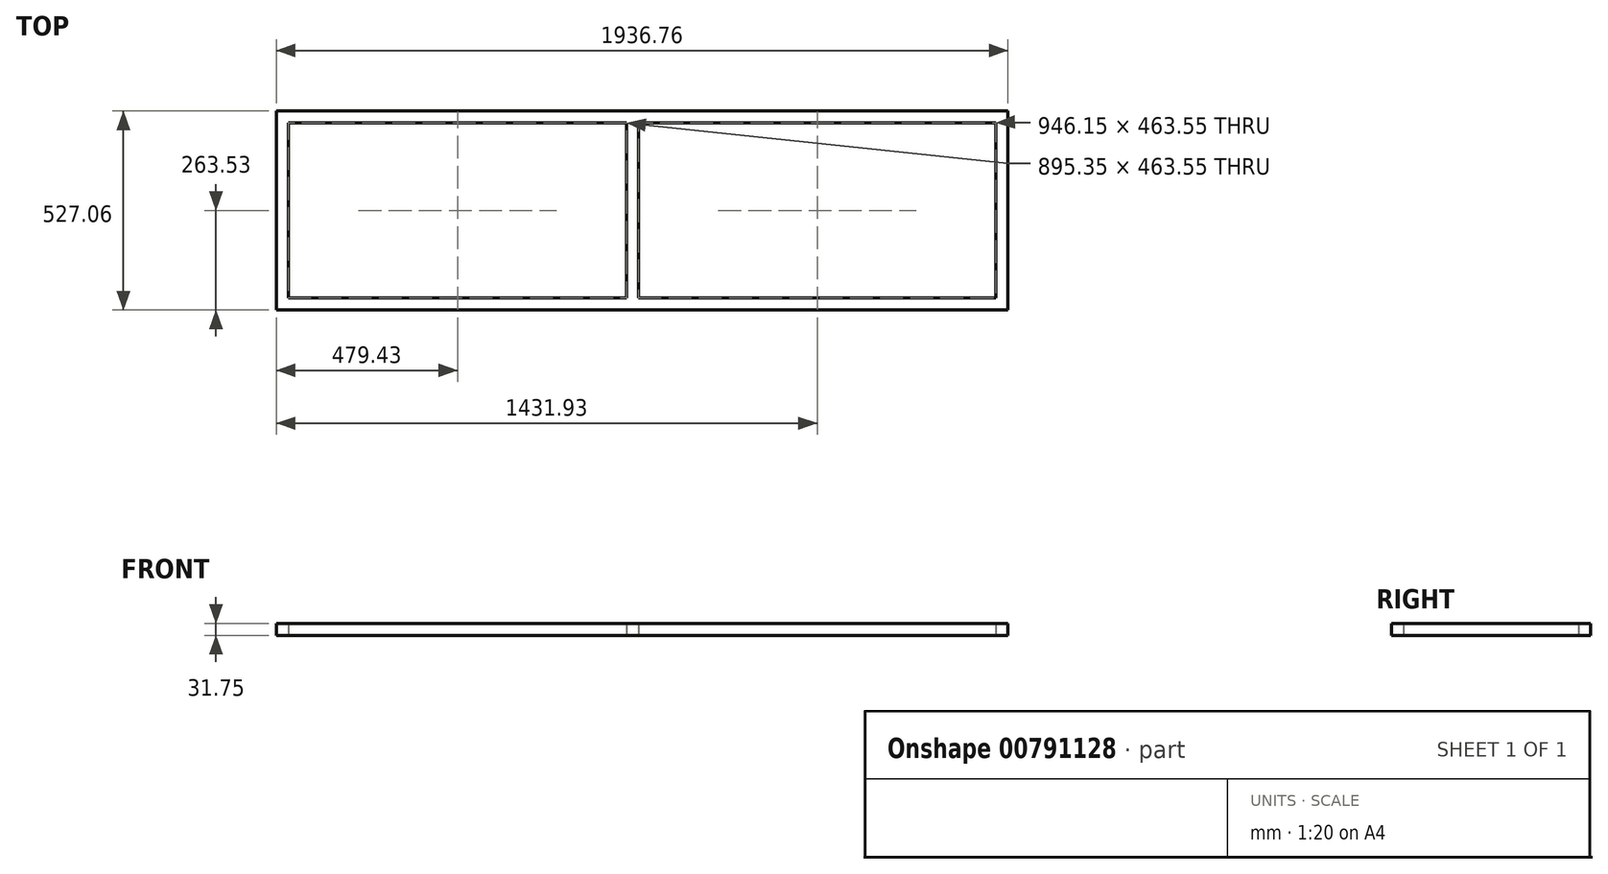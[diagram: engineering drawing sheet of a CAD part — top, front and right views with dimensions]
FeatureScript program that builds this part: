
annotation { "Feature Type Name" : "Feature", "Feature Type Description" : "" }
export const myFeature = defineFeature(function(context is Context, id is Id, definition is map)
    precondition{}
    {
        {
            var Q0;
            Q0=qCreatedBy(makeId("Top.planeOp"),FACE);
            cPlane(context, id + "F0", {"entities" : qUnion([Q0]), "cplaneType" : CPlaneType.OFFSET, "offset" : 254 * mm, "width" : 152.4 * mm, "height" : 152.4 * mm});
        }
        {
            var Q0;
            Q0=qCreatedBy(id+"F0.planeOp",FACE);
            var sketch = newSketch(context, id + "F1", { "sketchPlane" : qUnion([Q0])});
            skLineSegment(sketch, "E0.bottom", {"start": v(447.68, 231.77) * mm, "end": v(-447.68, 231.77) * mm});
            skLineSegment(sketch, "E0.top", {"start": v(447.68, -231.77) * mm, "end": v(-447.68, -231.77) * mm});
            skLineSegment(sketch, "E0.left", {"start": v(447.68, 231.78) * mm, "end": v(447.68, -231.78) * mm});
            skLineSegment(sketch, "E0.right", {"start": v(-447.68, 231.77) * mm, "end": v(-447.68, -231.77) * mm});
            skPoint(sketch, "E0.middle", {"position": v(0, 0) * mm});
            skLineSegment(sketch, "E1.bottom", {"start": v(479.43, 263.53) * mm, "end": v(-479.43, 263.52) * mm});
            skLineSegment(sketch, "E1.top", {"start": v(479.43, -263.52) * mm, "end": v(-479.43, -263.53) * mm});
            skLineSegment(sketch, "E1.right", {"start": v(-479.43, 263.52) * mm, "end": v(-479.43, -263.53) * mm});
            skLineSegment(sketch, "E2.bottom", {"start": v(479.43, -263.52) * mm, "end": v(1457.33, -263.52) * mm});
            skLineSegment(sketch, "E2.top", {"start": v(479.42, 263.53) * mm, "end": v(1457.33, 263.53) * mm});
            skLineSegment(sketch, "E2.left", {"start": v(479.43, -231.77) * mm, "end": v(479.43, 231.78) * mm});
            skLineSegment(sketch, "E2.right", {"start": v(1457.33, -263.52) * mm, "end": v(1457.33, 263.53) * mm});
            skLineSegment(sketch, "E3.bottom", {"start": v(479.43, -231.77) * mm, "end": v(1425.58, -231.77) * mm});
            skLineSegment(sketch, "E3.top", {"start": v(479.43, 231.78) * mm, "end": v(1425.58, 231.78) * mm});
            skLineSegment(sketch, "E3.right", {"start": v(1425.58, -231.77) * mm, "end": v(1425.58, 231.78) * mm});
            skSolve(sketch);
        }
        {
            var Q0;
            Q0 = qSketchRegion(id + "F1", true);
            extrude(context, id + "F2", {"entities" : qUnion([Q0]), "depth" : 31.75 * mm, "offsetDistance" : 25.4 * mm});
        }
    });
